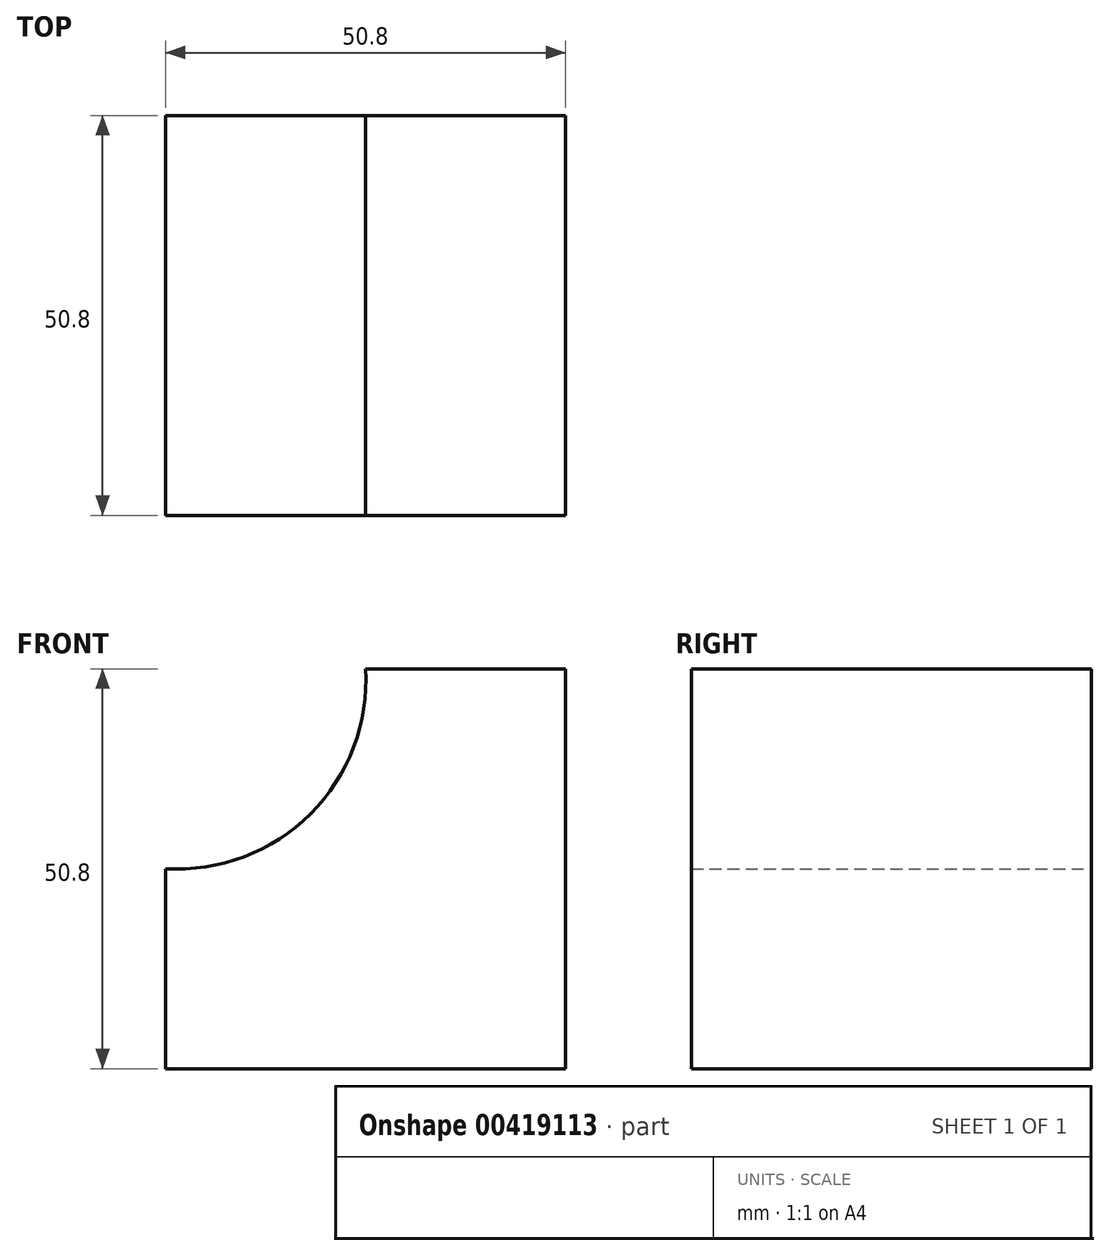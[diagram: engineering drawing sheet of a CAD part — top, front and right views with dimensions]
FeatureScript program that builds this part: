
annotation { "Feature Type Name" : "Feature", "Feature Type Description" : "" }
export const myFeature = defineFeature(function(context is Context, id is Id, definition is map)
    precondition{}
    {
        {
            var Q0;
            Q0=qCreatedBy(makeId("Front.planeOp"),FACE);
            var sketch = newSketch(context, id + "F0", { "sketchPlane" : qUnion([Q0])});
            skLineSegment(sketch, "E0", {"start": v(0, 0) * mm, "end": v(-50.8, 0) * mm});
            skLineSegment(sketch, "E1", {"start": v(0, 0) * mm, "end": v(0, 50.8) * mm});
            skLineSegment(sketch, "E2", {"start": v(0, 50.8) * mm, "end": v(-25.4, 50.8) * mm});
            skLineSegment(sketch, "E3", {"start": v(-50.8, 0) * mm, "end": v(-50.8, 25.4) * mm});
            skArc(sketch, "E4", {"start": v(-50.8, 25.4) * mm, "mid": v(-32.38, 32.38) * mm, "end": v(-25.4, 50.8) * mm});
            skSolve(sketch);
        }
        {
            var Q0;
            Q0 = qSketchRegion(id + "F0", true);
            extrude(context, id + "F1", {"entities" : qUnion([Q0]), "depth" : 50.8 * mm});
        }
    });
